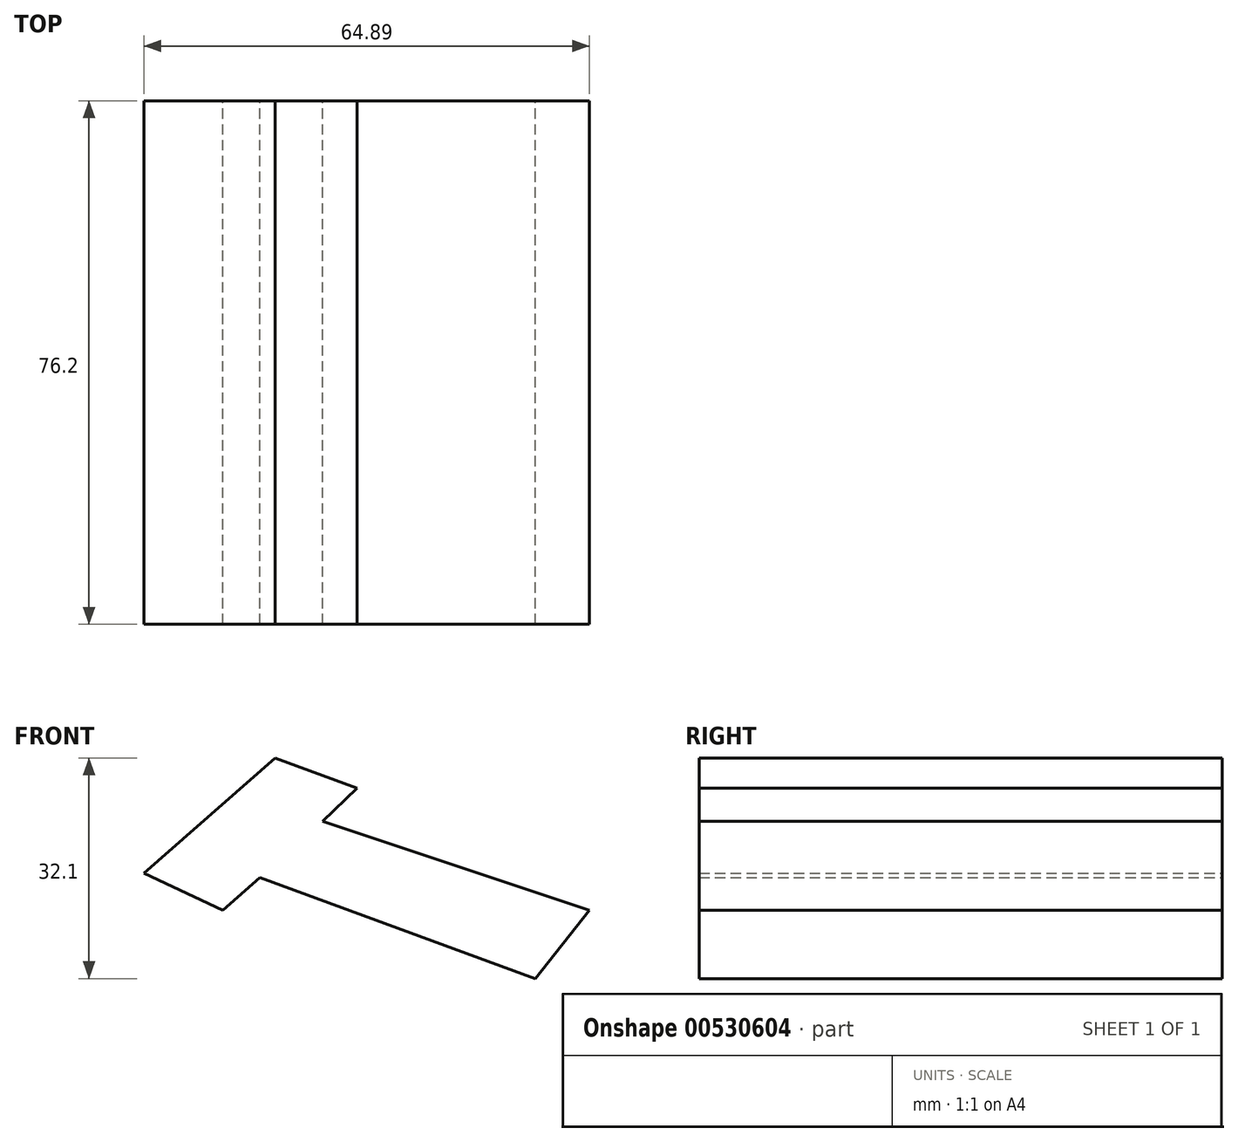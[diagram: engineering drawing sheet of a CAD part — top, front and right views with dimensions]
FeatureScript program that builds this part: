
annotation { "Feature Type Name" : "Feature", "Feature Type Description" : "" }
export const myFeature = defineFeature(function(context is Context, id is Id, definition is map)
    precondition{}
    {
        {
            var Q0;
            Q0=qCreatedBy(makeId("Front.planeOp"),FACE);
            var sketch = newSketch(context, id + "F0", { "sketchPlane" : qUnion([Q0])});
            skLineSegment(sketch, "E0", {"start": v(-98.23, 15.36) * mm, "end": v(-86.74, 9.95) * mm});
            skLineSegment(sketch, "E1", {"start": v(-86.74, 9.95) * mm, "end": v(-81.33, 14.68) * mm});
            skLineSegment(sketch, "E2", {"start": v(-81.33, 14.68) * mm, "end": v(-41.23, 0) * mm});
            skLineSegment(sketch, "E3", {"start": v(-41.23, 0) * mm, "end": v(-33.34, 9.95) * mm});
            skLineSegment(sketch, "E4", {"start": v(-98.23, 15.36) * mm, "end": v(-79.13, 32.1) * mm});
            skLineSegment(sketch, "E5", {"start": v(-79.13, 32.1) * mm, "end": v(-67.2, 27.74) * mm});
            skLineSegment(sketch, "E6", {"start": v(-67.2, 27.74) * mm, "end": v(-72.23, 22.93) * mm});
            skLineSegment(sketch, "E7", {"start": v(-72.23, 22.93) * mm, "end": v(-33.34, 9.95) * mm});
            skSolve(sketch);
        }
        {
            var Q0;
            Q0 = qSketchRegion(id + "F0", true);
            extrude(context, id + "F1", {"entities" : qUnion([Q0]), "depth" : 38.1 * mm, "offsetDistance" : 25.4 * mm});
        }
        {
            var Q0;
            Q0=makeQuery(id+"F1.opExtrude","CAP_FACE",FACE,{"disambiguationData":[OSD([sQuery(id+"F0.wireOp",EDGE,"E0"),sQuery(id+"F0.wireOp",EDGE,"E1"),sQuery(id+"F0.wireOp",EDGE,"E2"),sQuery(id+"F0.wireOp",EDGE,"E3"),sQuery(id+"F0.wireOp",EDGE,"E4"),sQuery(id+"F0.wireOp",EDGE,"E5"),sQuery(id+"F0.wireOp",EDGE,"E6"),sQuery(id+"F0.wireOp",EDGE,"E7")])],"isStart":false});
            extrude(context, id + "F2", {"entities" : qUnion([Q0]), "operationType" : NewBodyOperationType.ADD, "depth" : 38.1 * mm, "offsetDistance" : 25.4 * mm});
        }
    });
